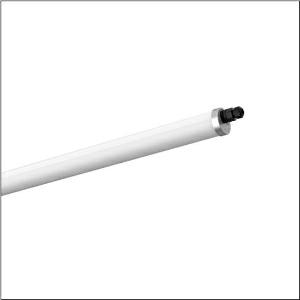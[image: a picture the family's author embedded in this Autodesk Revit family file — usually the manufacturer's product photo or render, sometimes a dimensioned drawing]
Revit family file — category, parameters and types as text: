
# Revit family: monsun_r__31_tube_51ft10dn460a_a449
name_source: partatom
category: Lighting Fixtures
units: mm (PartAtom-declared; Revit-internal decimal feet)

## family parameters
Cut with Voids When Loaded = No
Host = Face
Light Source = No
Part Type = Normal
Room Calculation Point = No
Round Connector Dimension = Use Diameter
Shared = No

## types (1)
- Monsun® 31 Tube (1 x LED, 6500 lm, 40 W, 4000K)
    Apparent Load = 40 VA
    CIE Flux Codes = 42 71 90 91 100
    Color Rendering = 80
    Color Temperature = 4000K
    Default Elevation = 1800 mm
    Description = Monsun® 31 Tube, tubular luminaire, primary optical cover: diffuser, of PMMA, light emission: direct distribution, primary light characteristic: symmetric, installation type: suspended mounting, surface-mounted, LED, rated luminous flux: 6.500lm, luminous efficacy: 160lm/W, light colour: 840, colour temperature: 4000K, with with 1 terminal, 5-pole, max. 2.5mm², through-wiring: 5x 1.5mm², mains connection: 220..240V, AC, 50/60Hz, rated input power: 40W, housing, cylindrical, of PMMA, semi-transparent, matt white, with luminaire and ceiling fastening, V4A, mounting with brackets of stainless steel, length: 1.570mm, diameter: 75mm, end cap, of stainless steel (V4A), protection rating (complete): IP67/IP69K, insulation class (complete): insulation class I (protective earthing), certification: CE, UKCA, impact resistance: IK07, permissible operating ambient temperature: -20..+40°C, corresponds to IFS (International Featured Standards) requirements for safety and quality in the food industry, usage in unprotected outdoor area possible with horizontal mounting, contact your sales advisor before using the luminaires in applications with unclear chemical exposure, large temperature fluctuations or condensation-forming humidity, packaging unit: 1 piece
    Height = 83 mm
    Lamp = 1 x LED
    Lamp Light Flux = 6500 lm
    Lamp Power = 40 W
    Lamp count = 1
    Length = 1570 mm
    Luminous efficacy = 163 lm/W
    Manufacturer = Siteco
    ModVariant = No
    Model = 51FT10DN460A
    Mounting Place = Ceiling
    Mounting Type = Pendant
    Number of Poles = 1
    OnlyDefault = Yes
    Power Factor = 1
    Product Name = Monsun® 31 Tube
    Product group = tubular luminaire
    ProductGroupID = 906
    Protection Class = Protection class I
    RLX_Detail_Level = 1
    RLX_Emergency_Light_Flux = 0 lm
    RLX_Emergency_Type = 0
    RLX_Emergency_Type_DB = No
    RlxData = <blob elided: 25221 chars, md5=7a8dbe58>
    Socket = socket
    Standby Power = 0 W
    System Light Flux = 6500 lm
    System Power = 40 W
    Type Comments = Product without accessories
    Type Image = l_1228461.jpg
    URL = http://relux.com
    VarID = ---
    Voltage = 0 V
    Weight = 0.00 kg
    Width = 75 mm

## geometry (parser evidence)
native form markers: Blend x4, Sweep x13
no freeform markers — native parametric forms only
